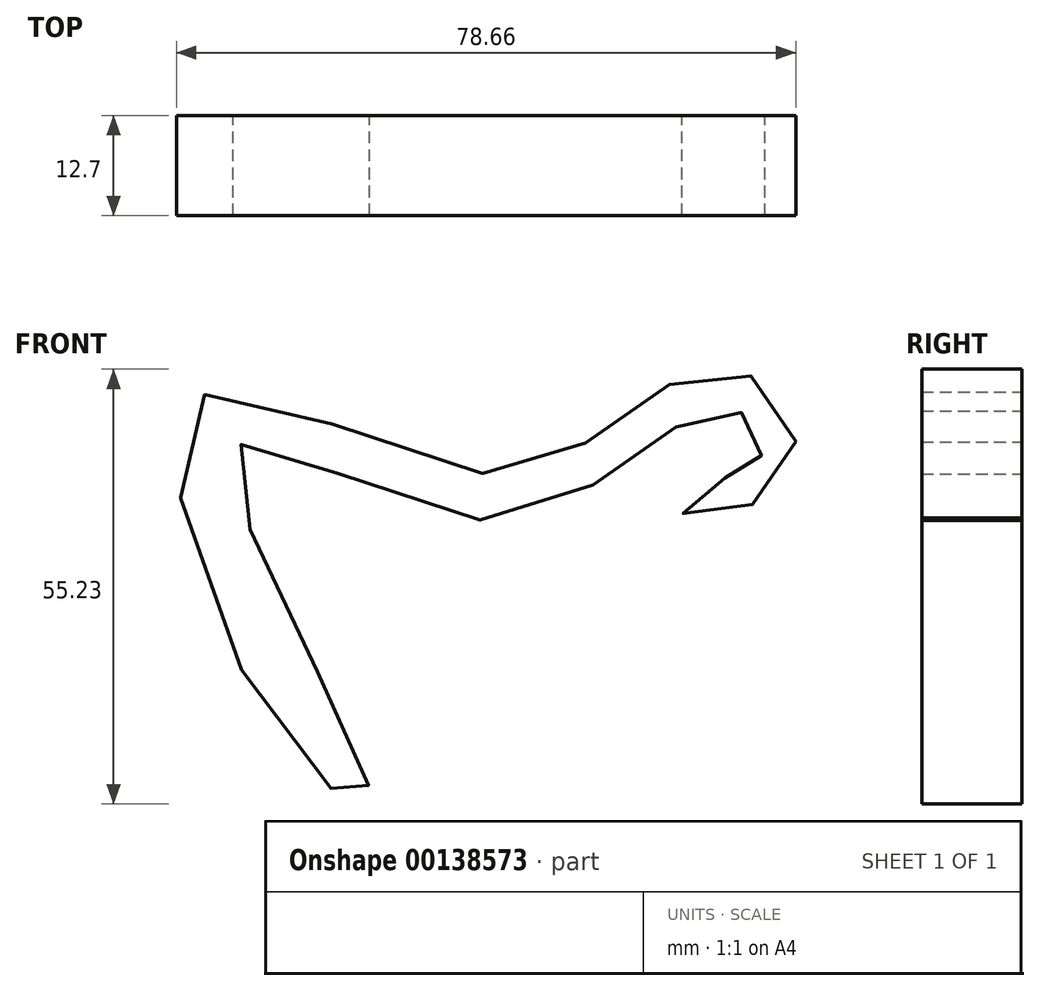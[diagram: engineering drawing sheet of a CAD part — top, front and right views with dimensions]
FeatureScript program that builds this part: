
annotation { "Feature Type Name" : "Feature", "Feature Type Description" : "" }
export const myFeature = defineFeature(function(context is Context, id is Id, definition is map)
    precondition{}
    {
        {
            var Q0;
            Q0=qCreatedBy(makeId("Front.planeOp"),FACE);
            var sketch = newSketch(context, id + "F0", { "sketchPlane" : qUnion([Q0])});
            skFitSpline(sketch, "E0", {"points": [v(31.4, -4.42) * mm, v(25.9, -8.64) * mm, v(33.1, -8.62) * mm, v(40.38, 0) * mm, v(33.3, 9.06) * mm, v(19.4, 4.27) * mm, v(0, -3.8) * mm, v(-35.92, 5.5) * mm, v(-25.78, -35.95) * mm, v(-13.94, -45.4) * mm, v(-25.58, -18.65) * mm, v(-29.69, 0) * mm, v(0, -9.78) * mm, v(21.97, 0) * mm, v(31.95, 4.08) * mm, v(36.34, 1.47) * mm, v(34.68, -3.64) * mm, v(31.4, -4.42) * mm]});
            skSolve(sketch);
        }
        {
            var Q0;
            Q0=makeQuery(id+"F0.imprint","IMPRINT",FACE,{"disambiguationData":[TD([[makeQuery(id+"F0.imprint","IMPRINT",EDGE,{"derivedFrom":sQuery(id+"F0.wireOp",EDGE,"E0")}),1.0]])]});
            extrude(context, id + "F1", {"entities" : qUnion([Q0]), "depth" : 12.7 * mm});
        }
    });
